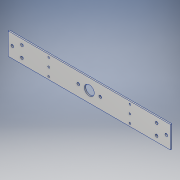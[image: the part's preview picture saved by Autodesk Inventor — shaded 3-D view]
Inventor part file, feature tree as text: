
AUTODESK INVENTOR PART (.ipt)
format: ipt  version: 2017 (Build 210142000, 142)  size: 147,968 bytes
history: native  units: in
note: dims shown in document units (in); Inventor stores cm internally (conversion verified against a paired STEP export)
features: hole x3, sketch x3, extrude x1
ambient origin geometry x8: Origin, YZ Plane, XZ Plane, XY Plane, X Axis, Y Axis, Z Axis, Center Point
bodies: Body1 (feature_tree)
feature tree (7):
  extrude  "Extrusion2"  Depth=14.75in
  hole  "Hole1"  [1 undecoded]
  hole  "Hole2"  [1 undecoded]
  hole  "Hole3"  [1 undecoded]
  sketch  "Sketch3"  dims[d0=14.75in d3=0.5in]
  sketch  "Sketch4"  dims[d4=1.0in d5=0.25in]
  sketch  "Sketch5"  dims[d6=0.25in d10=0.25in d11=1.25in d12=0.125in d13=0.0in d14=0.9in d15=0.75in d16=0.375in d17=0.25in d18=0.5635in d19=1.0in d20=0.8108in d21=1.0in d22=0.25in d23=0.25in d24=0.75in d25=0.375in d26=0.25in d27=0.5635in d28=1.0in d29=0.8108in d30=3.689in d31=0.25in d32=0.75in d33=0.163in d34=0.75in d35=0.163in d36=0.163in d37=0.163in d38=0.75in d39=0.375in d40=0.25in d41=0.5635in d42=1.0in d43=0.8108in]
note: 3 required parameter values undecoded (feature->parameter linkage not recoverable at this tier; creation-order binding heuristic only, values carry confidence <= 0.55)
